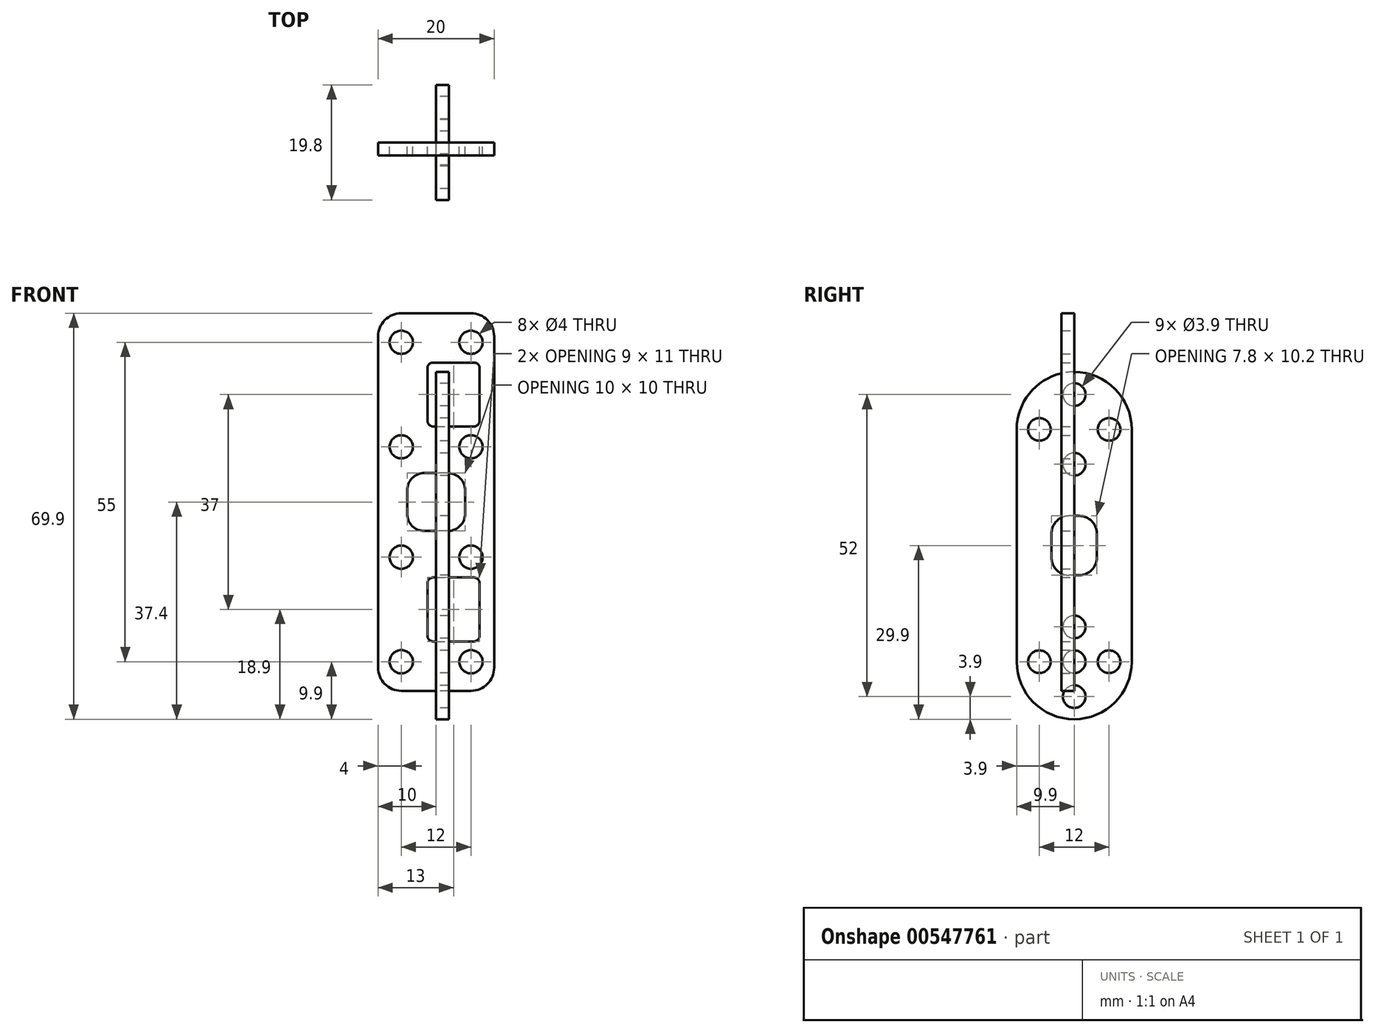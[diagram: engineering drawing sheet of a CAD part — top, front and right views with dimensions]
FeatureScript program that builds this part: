
annotation { "Feature Type Name" : "Feature", "Feature Type Description" : "" }
export const myFeature = defineFeature(function(context is Context, id is Id, definition is map)
    precondition{}
    {
        {
            assignVariable(context, id + "F0", {"name" : "thickness", "anyValue" : 2.2});
        }
        {
            var Q0;
            Q0=qCreatedBy(makeId("Right.planeOp"),FACE);
            var sketch = newSketch(context, id + "F1", { "sketchPlane" : qUnion([Q0])});
            skLineSegment(sketch, "E0.rect.bottom", {"start": v(12, -9) * mm, "end": v(-12, -9) * mm});
            skLineSegment(sketch, "E0.rect.top", {"start": v(12, 27) * mm, "end": v(-12, 27) * mm});
            skLineSegment(sketch, "E0.rect.left", {"start": v(12, -9) * mm, "end": v(12, 27) * mm});
            skLineSegment(sketch, "E0.rect.right", {"start": v(-12, -9) * mm, "end": v(-12, 27) * mm});
            skPoint(sketch, "E0.rect.middle", {"position": v(0, 9) * mm});
            skCircle(sketch, "E1", {"center": v(0, 0) * mm, "radius": 8.9 * mm});
            skLineSegment(sketch, "E2", {"start": v(0, 27) * mm, "end": v(0, -9) * mm, "construction": true});
            skCircle(sketch, "E3", {"center": v(0, 0) * mm, "radius": 6 * mm, "construction": true});
            skCircle(sketch, "E4", {"center": v(0, -6) * mm, "radius": 1.95 * mm});
            skCircle(sketch, "E5.1.0", {"center": v(6, 0) * mm, "radius": 1.95 * mm});
            skCircle(sketch, "E5.2.0", {"center": v(0, 6) * mm, "radius": 1.95 * mm});
            skCircle(sketch, "E5.3.0", {"center": v(-6, 0) * mm, "radius": 1.95 * mm});
            skCircle(sketch, "E6", {"center": v(-4.24, 4.24) * mm, "radius": 0.8 * mm});
            skCircle(sketch, "E7.1.0", {"center": v(-4.24, -4.24) * mm, "radius": 0.8 * mm});
            skCircle(sketch, "E7.2.0", {"center": v(4.24, -4.24) * mm, "radius": 0.8 * mm});
            skCircle(sketch, "E7.3.0", {"center": v(4.24, 4.24) * mm, "radius": 0.8 * mm});
            skLineSegment(sketch, "E8", {"start": v(-6, 24) * mm, "end": v(6, 24) * mm, "construction": true});
            skCircle(sketch, "E9", {"center": v(-6, 24) * mm, "radius": 1.95 * mm});
            skCircle(sketch, "E10", {"center": v(0, 24) * mm, "radius": 1.95 * mm});
            skCircle(sketch, "E11", {"center": v(6, 24) * mm, "radius": 1.95 * mm});
            skPoint(sketch, "E12.center", {"position": v(0, 55) * mm});
            skLineSegment(sketch, "E13.rect.right", {"start": v(12, 64) * mm, "end": v(12, 28) * mm});
            skCircle(sketch, "E14", {"center": v(-6, 31) * mm, "radius": 1.95 * mm});
            skLineSegment(sketch, "E15", {"start": v(0, 28) * mm, "end": v(0, 64) * mm, "construction": true});
            skCircle(sketch, "E16", {"center": v(0, 55) * mm, "radius": 8.9 * mm});
            skLineSegment(sketch, "E13.rect.left", {"start": v(-12, 64) * mm, "end": v(-12, 28) * mm});
            skLineSegment(sketch, "E13.rect.bottom", {"start": v(-12, 64) * mm, "end": v(12, 64) * mm});
            skLineSegment(sketch, "E13.rect.top", {"start": v(-12, 28) * mm, "end": v(12, 28) * mm});
            skLineSegment(sketch, "E17", {"start": v(6, 31) * mm, "end": v(-6, 31) * mm, "construction": true});
            skCircle(sketch, "E18", {"center": v(0, 31) * mm, "radius": 1.95 * mm});
            skPoint(sketch, "E13.rect.middle", {"position": v(0, 46) * mm});
            skCircle(sketch, "E12.2.0", {"center": v(0, 49) * mm, "radius": 1.95 * mm});
            skCircle(sketch, "E12.1.0", {"center": v(-6, 55) * mm, "radius": 1.95 * mm});
            skCircle(sketch, "E19", {"center": v(0, 55) * mm, "radius": 6 * mm, "construction": true});
            skCircle(sketch, "E20", {"center": v(0, 61) * mm, "radius": 1.95 * mm});
            skCircle(sketch, "E21", {"center": v(-4.24, 59.24) * mm, "radius": 0.8 * mm});
            skCircle(sketch, "E12.3.0", {"center": v(6, 55) * mm, "radius": 1.95 * mm});
            skCircle(sketch, "E22.3.0", {"center": v(4.24, 59.24) * mm, "radius": 0.8 * mm});
            skCircle(sketch, "E22.2.0", {"center": v(4.24, 50.76) * mm, "radius": 0.8 * mm});
            skCircle(sketch, "E22.1.0", {"center": v(-4.24, 50.76) * mm, "radius": 0.8 * mm});
            skCircle(sketch, "E23", {"center": v(6, 31) * mm, "radius": 1.95 * mm});
            skSolve(sketch);
        }
        {
            var Q0;
            Q0=qCreatedBy(makeId("Front.planeOp"),FACE);
            var sketch = newSketch(context, id + "F2", { "sketchPlane" : qUnion([Q0])});
            skLineSegment(sketch, "E24", {"start": v(0, 22.5) * mm, "end": v(9, 22.5) * mm});
            skLineSegment(sketch, "E25", {"start": v(9, 22.5) * mm, "end": v(9, 27) * mm});
            skLineSegment(sketch, "E26", {"start": v(9, 27) * mm, "end": v(12, 27) * mm});
            skLineSegment(sketch, "E27", {"start": v(12, 27) * mm, "end": v(12, -9) * mm});
            skLineSegment(sketch, "E28", {"start": v(12, -9) * mm, "end": v(0, -9) * mm});
            skLineSegment(sketch, "E29", {"start": v(12, 8.9) * mm, "end": v(15, 8.9) * mm});
            skLineSegment(sketch, "E30", {"start": v(15, 8.9) * mm, "end": v(15, -8.9) * mm});
            skLineSegment(sketch, "E31", {"start": v(15, -8.9) * mm, "end": v(12, -8.9) * mm});
            skLineSegment(sketch, "E32", {"start": v(0, 1.45) * mm, "end": v(0, -56.88) * mm, "construction": true});
            skLineSegment(sketch, "E33", {"start": v(0, 0) * mm, "end": v(15, 0) * mm, "construction": true});
            skLineSegment(sketch, "E34.MirrorCS", {"start": v(-15, 8.9) * mm, "end": v(-15, -8.9) * mm});
            skLineSegment(sketch, "E35.MirrorCS", {"start": v(0, 22.5) * mm, "end": v(-9, 22.5) * mm});
            skLineSegment(sketch, "E36.MirrorCS", {"start": v(0, 0) * mm, "end": v(-15, 0) * mm, "construction": true});
            skLineSegment(sketch, "E37.MirrorCS", {"start": v(-9, 22.5) * mm, "end": v(-9, 27) * mm});
            skLineSegment(sketch, "E38.MirrorCS", {"start": v(-12, 8.9) * mm, "end": v(-15, 8.9) * mm});
            skLineSegment(sketch, "E39.MirrorCS", {"start": v(-12, -9) * mm, "end": v(0, -9) * mm});
            skLineSegment(sketch, "E40.MirrorCS", {"start": v(-12, 27) * mm, "end": v(-12, -9) * mm});
            skLineSegment(sketch, "E41.MirrorCS", {"start": v(-15, -8.9) * mm, "end": v(-12, -8.9) * mm});
            skLineSegment(sketch, "E42.MirrorCS", {"start": v(-9, 27) * mm, "end": v(-12, 27) * mm});
            skLineSegment(sketch, "E43.MirrorCS", {"start": v(0, 55) * mm, "end": v(-15, 55) * mm, "construction": true});
            skLineSegment(sketch, "E44.MirrorCS", {"start": v(0, 32.5) * mm, "end": v(-9, 32.5) * mm});
            skLineSegment(sketch, "E45", {"start": v(15, 63.9) * mm, "end": v(15, 46.1) * mm});
            skLineSegment(sketch, "E46.MirrorCS", {"start": v(-15, 63.9) * mm, "end": v(-15, 46.1) * mm});
            skLineSegment(sketch, "E47", {"start": v(0, 57.8) * mm, "end": v(0, 0) * mm, "construction": true});
            skLineSegment(sketch, "E48", {"start": v(12, 64) * mm, "end": v(0, 64) * mm});
            skLineSegment(sketch, "E49", {"start": v(12, 64) * mm, "end": v(12, 28) * mm});
            skLineSegment(sketch, "E50", {"start": v(0, 32.5) * mm, "end": v(9, 32.5) * mm});
            skLineSegment(sketch, "E51.MirrorCS", {"start": v(-12, 64) * mm, "end": v(0, 64) * mm});
            skLineSegment(sketch, "E52.MirrorCS", {"start": v(-12, 64) * mm, "end": v(-12, 28) * mm});
            skLineSegment(sketch, "E53", {"start": v(0, 55) * mm, "end": v(15, 55) * mm, "construction": true});
            skLineSegment(sketch, "E54", {"start": v(12, 63.9) * mm, "end": v(15, 63.9) * mm});
            skLineSegment(sketch, "E55", {"start": v(9, 28) * mm, "end": v(12, 28) * mm});
            skLineSegment(sketch, "E56", {"start": v(9, 28) * mm, "end": v(9, 32.5) * mm});
            skLineSegment(sketch, "E57.MirrorCS", {"start": v(-9, 28) * mm, "end": v(-12, 28) * mm});
            skLineSegment(sketch, "E58.MirrorCS", {"start": v(-12, 63.9) * mm, "end": v(-15, 63.9) * mm});
            skLineSegment(sketch, "E59.MirrorCS", {"start": v(-9, 28) * mm, "end": v(-9, 32.5) * mm});
            skLineSegment(sketch, "E60.MirrorCS", {"start": v(-15, 46.1) * mm, "end": v(-12, 46.1) * mm});
            skLineSegment(sketch, "E61", {"start": v(15, 46.1) * mm, "end": v(12, 46.1) * mm});
            skLineSegment(sketch, "E62.bottom", {"start": v(-6, 18) * mm, "end": v(6, 18) * mm, "construction": true});
            skLineSegment(sketch, "E62.top", {"start": v(-6, 0) * mm, "end": v(6, 0) * mm, "construction": true});
            skLineSegment(sketch, "E62.left", {"start": v(-6, 18) * mm, "end": v(-6, 0) * mm, "construction": true});
            skLineSegment(sketch, "E62.right", {"start": v(6, 18) * mm, "end": v(6, 0) * mm, "construction": true});
            skCircle(sketch, "E63", {"center": v(6, 0) * mm, "radius": 2 * mm});
            skCircle(sketch, "E64", {"center": v(-6, 0) * mm, "radius": 2 * mm});
            skCircle(sketch, "E65", {"center": v(-6, 18) * mm, "radius": 2 * mm});
            skCircle(sketch, "E66", {"center": v(6, 18) * mm, "radius": 2 * mm});
            skLineSegment(sketch, "E67.left", {"start": v(-6, 55) * mm, "end": v(-6, 37) * mm, "construction": true});
            skCircle(sketch, "E68", {"center": v(-6, 55) * mm, "radius": 2 * mm});
            skLineSegment(sketch, "E67.right", {"start": v(6, 55) * mm, "end": v(6, 37) * mm, "construction": true});
            skLineSegment(sketch, "E67.bottom", {"start": v(-6, 55) * mm, "end": v(6, 55) * mm, "construction": true});
            skCircle(sketch, "E69", {"center": v(6, 55) * mm, "radius": 2 * mm});
            skCircle(sketch, "E70", {"center": v(6, 37) * mm, "radius": 2 * mm});
            skLineSegment(sketch, "E67.top", {"start": v(-6, 37) * mm, "end": v(6, 37) * mm, "construction": true});
            skCircle(sketch, "E71", {"center": v(-6, 37) * mm, "radius": 2 * mm});
            skLineSegment(sketch, "E72.rect.bottom", {"start": v(7.5, 51.5) * mm, "end": v(-7.5, 51.5) * mm});
            skLineSegment(sketch, "E72.rect.top", {"start": v(7.5, 40.5) * mm, "end": v(-7.5, 40.5) * mm});
            skLineSegment(sketch, "E72.rect.left", {"start": v(7.5, 51.5) * mm, "end": v(7.5, 40.5) * mm});
            skLineSegment(sketch, "E72.rect.right", {"start": v(-7.5, 51.5) * mm, "end": v(-7.5, 40.5) * mm});
            skPoint(sketch, "E72.rect.middle", {"position": v(0, 46) * mm});
            skLineSegment(sketch, "E73.rect.bottom", {"start": v(7.5, 3.5) * mm, "end": v(-7.5, 3.5) * mm});
            skLineSegment(sketch, "E73.rect.top", {"start": v(7.5, 14.5) * mm, "end": v(-7.5, 14.5) * mm});
            skLineSegment(sketch, "E73.rect.left", {"start": v(7.5, 3.5) * mm, "end": v(7.5, 14.5) * mm});
            skLineSegment(sketch, "E73.rect.right", {"start": v(-7.5, 3.5) * mm, "end": v(-7.5, 14.5) * mm});
            skPoint(sketch, "E73.rect.middle", {"position": v(0, 9) * mm});
            skSolve(sketch);
        }
        {
            var Q0;
            Q0=qCreatedBy(makeId("Front.planeOp"),FACE);
            var sketch = newSketch(context, id + "F3", { "sketchPlane" : qUnion([Q0])});
            skLineSegment(sketch, "E74.rect.bottom", {"start": v(6, 60) * mm, "end": v(-6, 60) * mm});
            skLineSegment(sketch, "E74.rect.top", {"start": v(6, -5) * mm, "end": v(-6, -5) * mm});
            skLineSegment(sketch, "E74.rect.left", {"start": v(10, 56) * mm, "end": v(10, -1) * mm});
            skLineSegment(sketch, "E74.rect.right", {"start": v(-10, 56) * mm, "end": v(-10, -1) * mm});
            skPoint(sketch, "E74.rect.middle", {"position": v(0, 27.5) * mm});
            skCircle(sketch, "E75", {"center": v(-6, 18) * mm, "radius": 2 * mm});
            skCircle(sketch, "E76", {"center": v(6, 18) * mm, "radius": 2 * mm});
            skCircle(sketch, "E77", {"center": v(-6, 0) * mm, "radius": 2 * mm});
            skCircle(sketch, "E78", {"center": v(6, 0) * mm, "radius": 2 * mm});
            skCircle(sketch, "E79", {"center": v(-6, 37) * mm, "radius": 2 * mm});
            skCircle(sketch, "E80", {"center": v(6, 37) * mm, "radius": 2 * mm});
            skCircle(sketch, "E81", {"center": v(-6, 55) * mm, "radius": 2 * mm});
            skCircle(sketch, "E82", {"center": v(6, 55) * mm, "radius": 2 * mm});
            skPoint(sketch, "E83.visualSharp", {"position": v(-10, 60) * mm});
            skArc(sketch, "E83.filletArc", {"start": v(-6, 60) * mm, "mid": v(-8.83, 58.83) * mm, "end": v(-10, 56) * mm});
            skPoint(sketch, "E84.visualSharp", {"position": v(10, 60) * mm});
            skArc(sketch, "E84.filletArc", {"start": v(10, 56) * mm, "mid": v(8.83, 58.83) * mm, "end": v(6, 60) * mm});
            skPoint(sketch, "E85.visualSharp", {"position": v(10, -5) * mm});
            skArc(sketch, "E85.filletArc", {"start": v(6, -5) * mm, "mid": v(8.83, -3.83) * mm, "end": v(10, -1) * mm});
            skPoint(sketch, "E86.visualSharp", {"position": v(-10, -5) * mm});
            skArc(sketch, "E86.filletArc", {"start": v(-10, -1) * mm, "mid": v(-8.83, -3.83) * mm, "end": v(-6, -5) * mm});
            skLineSegment(sketch, "E87.rect.bottom", {"start": v(2, 22.5) * mm, "end": v(-2, 22.5) * mm});
            skLineSegment(sketch, "E87.rect.top", {"start": v(2, 32.5) * mm, "end": v(-2, 32.5) * mm});
            skLineSegment(sketch, "E87.rect.left", {"start": v(5, 25.5) * mm, "end": v(5, 29.5) * mm});
            skLineSegment(sketch, "E87.rect.right", {"start": v(-5, 25.5) * mm, "end": v(-5, 29.5) * mm});
            skPoint(sketch, "E88.visualSharp", {"position": v(-5, 32.5) * mm});
            skArc(sketch, "E88.filletArc", {"start": v(-2, 32.5) * mm, "mid": v(-4.12, 31.62) * mm, "end": v(-5, 29.5) * mm});
            skPoint(sketch, "E89.visualSharp", {"position": v(5, 32.5) * mm});
            skArc(sketch, "E89.filletArc", {"start": v(5, 29.5) * mm, "mid": v(4.12, 31.62) * mm, "end": v(2, 32.5) * mm});
            skPoint(sketch, "E90.visualSharp", {"position": v(5, 22.5) * mm});
            skArc(sketch, "E90.filletArc", {"start": v(2, 22.5) * mm, "mid": v(4.12, 23.38) * mm, "end": v(5, 25.5) * mm});
            skPoint(sketch, "E91.visualSharp", {"position": v(-5, 22.5) * mm});
            skArc(sketch, "E91.filletArc", {"start": v(-5, 25.5) * mm, "mid": v(-4.12, 23.38) * mm, "end": v(-2, 22.5) * mm});
            skSolve(sketch);
        }
        {
            var Q0;
            Q0=makeQuery(id+"F3.imprint","IMPRINT",FACE,{"disambiguationData":[TD([[makeQuery(id+"F3.imprint","IMPRINT",EDGE,{"derivedFrom":sQuery(id+"F3.wireOp",EDGE,"E74.rect.bottom")}),1.0]])]});
            extrude(context, id + "F4", {"entities" : qUnion([Q0]), "depth" : (getVariable(context, 'thickness')) * mm, "offsetDistance" : 25 * mm});
        }
        {
            var Q0;
            Q0=qCreatedBy(makeId("Front.planeOp"),FACE);
            var sketch = newSketch(context, id + "F5", { "sketchPlane" : qUnion([Q0])});
            skLineSegment(sketch, "E92.rect.bottom", {"start": v(-0.5, 14.5) * mm, "end": v(6.5, 14.5) * mm});
            skLineSegment(sketch, "E92.rect.top", {"start": v(-0.5, 3.5) * mm, "end": v(6.5, 3.5) * mm});
            skLineSegment(sketch, "E92.rect.left", {"start": v(-1.5, 13.5) * mm, "end": v(-1.5, 4.5) * mm});
            skLineSegment(sketch, "E92.rect.right", {"start": v(7.5, 13.5) * mm, "end": v(7.5, 4.5) * mm});
            skPoint(sketch, "E92.rect.middle", {"position": v(3, 9) * mm});
            skPoint(sketch, "E93.visualSharp", {"position": v(-1.5, 14.5) * mm});
            skArc(sketch, "E93.filletArc", {"start": v(-0.5, 14.5) * mm, "mid": v(-1.2, 14.2) * mm, "end": v(-1.5, 13.5) * mm});
            skPoint(sketch, "E94.visualSharp", {"position": v(7.5, 14.5) * mm});
            skArc(sketch, "E94.filletArc", {"start": v(7.5, 13.5) * mm, "mid": v(7.2, 14.2) * mm, "end": v(6.5, 14.5) * mm});
            skPoint(sketch, "E95.visualSharp", {"position": v(7.5, 3.5) * mm});
            skArc(sketch, "E95.filletArc", {"start": v(6.5, 3.5) * mm, "mid": v(7.2, 3.8) * mm, "end": v(7.5, 4.5) * mm});
            skPoint(sketch, "E96.visualSharp", {"position": v(-1.5, 3.5) * mm});
            skArc(sketch, "E96.filletArc", {"start": v(-1.5, 4.5) * mm, "mid": v(-1.2, 3.8) * mm, "end": v(-0.5, 3.5) * mm});
            skPoint(sketch, "E97.visualSharp", {"position": v(7.5, 51.5) * mm});
            skPoint(sketch, "E98.visualSharp", {"position": v(-1.5, 40.5) * mm});
            skPoint(sketch, "E99.rect.middle", {"position": v(3, 46) * mm});
            skPoint(sketch, "E100.visualSharp", {"position": v(7.5, 40.5) * mm});
            skLineSegment(sketch, "E99.rect.top", {"start": v(-0.5, 40.5) * mm, "end": v(6.5, 40.5) * mm});
            skLineSegment(sketch, "E99.rect.right", {"start": v(7.5, 50.5) * mm, "end": v(7.5, 41.5) * mm});
            skPoint(sketch, "E101.visualSharp", {"position": v(-1.5, 51.5) * mm});
            skLineSegment(sketch, "E99.rect.bottom", {"start": v(-0.5, 51.5) * mm, "end": v(6.5, 51.5) * mm});
            skLineSegment(sketch, "E99.rect.left", {"start": v(-1.5, 50.5) * mm, "end": v(-1.5, 41.5) * mm});
            skArc(sketch, "E98.filletArc", {"start": v(-1.5, 41.5) * mm, "mid": v(-1.2, 40.8) * mm, "end": v(-0.5, 40.5) * mm});
            skArc(sketch, "E101.filletArc", {"start": v(-0.5, 51.5) * mm, "mid": v(-1.2, 51.2) * mm, "end": v(-1.5, 50.5) * mm});
            skArc(sketch, "E97.filletArc", {"start": v(7.5, 50.5) * mm, "mid": v(7.2, 51.2) * mm, "end": v(6.5, 51.5) * mm});
            skArc(sketch, "E100.filletArc", {"start": v(6.5, 40.5) * mm, "mid": v(7.2, 40.8) * mm, "end": v(7.5, 41.5) * mm});
            skSolve(sketch);
        }
        {
            var Q0;
            Q0=qSketchRegion(id+"F5",true);
            extrude(context, id + "F6", {"entities" : qUnion([Q0]), "operationType" : NewBodyOperationType.REMOVE, "endBound" : BoundingType.UP_TO_NEXT, "depth" : 25 * mm});
        }
        {
            var Q0;
            Q0=qCreatedBy(makeId("Right.planeOp"),FACE);
            var sketch = newSketch(context, id + "F7", { "sketchPlane" : qUnion([Q0])});
            skCircle(sketch, "E102", {"center": v(0, 0) * mm, "radius": 9.9 * mm});
            skLineSegment(sketch, "E103", {"start": v(9.9, 0) * mm, "end": v(9.9, 40) * mm});
            skLineSegment(sketch, "E104", {"start": v(-9.9, 40) * mm, "end": v(-9.9, 0) * mm});
            skCircle(sketch, "E105", {"center": v(-6, 0) * mm, "radius": 1.95 * mm});
            skCircle(sketch, "E106", {"center": v(0, 6) * mm, "radius": 1.95 * mm});
            skCircle(sketch, "E107", {"center": v(6, 0) * mm, "radius": 1.95 * mm});
            skCircle(sketch, "E108", {"center": v(0, -6) * mm, "radius": 1.95 * mm});
            skCircle(sketch, "E109", {"center": v(0, 0) * mm, "radius": 1.95 * mm});
            skLineSegment(sketch, "E110.rect.bottom", {"start": v(0.9, 14.9) * mm, "end": v(-0.9, 14.9) * mm});
            skLineSegment(sketch, "E110.rect.top", {"start": v(0.9, 25.1) * mm, "end": v(-0.9, 25.1) * mm});
            skLineSegment(sketch, "E110.rect.left", {"start": v(3.9, 17.9) * mm, "end": v(3.9, 22.1) * mm});
            skLineSegment(sketch, "E110.rect.right", {"start": v(-3.9, 17.9) * mm, "end": v(-3.9, 22.1) * mm});
            skPoint(sketch, "E110.rect.middle", {"position": v(0, 20) * mm});
            skPoint(sketch, "E111.visualSharp", {"position": v(-3.9, 14.9) * mm});
            skArc(sketch, "E111.filletArc", {"start": v(-3.9, 17.9) * mm, "mid": v(-3.02, 15.78) * mm, "end": v(-0.9, 14.9) * mm});
            skPoint(sketch, "E112.visualSharp", {"position": v(3.9, 14.9) * mm});
            skArc(sketch, "E112.filletArc", {"start": v(0.9, 14.9) * mm, "mid": v(3.02, 15.78) * mm, "end": v(3.9, 17.9) * mm});
            skPoint(sketch, "E113.visualSharp", {"position": v(-3.9, 25.1) * mm});
            skArc(sketch, "E113.filletArc", {"start": v(-0.9, 25.1) * mm, "mid": v(-3.02, 24.22) * mm, "end": v(-3.9, 22.1) * mm});
            skPoint(sketch, "E114.visualSharp", {"position": v(3.9, 25.1) * mm});
            skArc(sketch, "E114.filletArc", {"start": v(3.9, 22.1) * mm, "mid": v(3.02, 24.22) * mm, "end": v(0.9, 25.1) * mm});
            skCircle(sketch, "E115", {"center": v(0, 40) * mm, "radius": 9.9 * mm});
            skCircle(sketch, "E116", {"center": v(0, 40) * mm, "radius": 6 * mm, "construction": true});
            skCircle(sketch, "E117", {"center": v(0, 46) * mm, "radius": 1.95 * mm});
            skCircle(sketch, "E118.1.0", {"center": v(-6, 40) * mm, "radius": 1.95 * mm});
            skCircle(sketch, "E118.2.0", {"center": v(0, 34) * mm, "radius": 1.95 * mm});
            skCircle(sketch, "E118.3.0", {"center": v(6, 40) * mm, "radius": 1.95 * mm});
            skSolve(sketch);
        }
        {
            var Q0;
            Q0=qSketchRegion(id+"F7",true);
            extrude(context, id + "F8", {"entities" : qUnion([Q0]), "depth" : (getVariable(context, 'thickness')) * mm});
        }
    });
